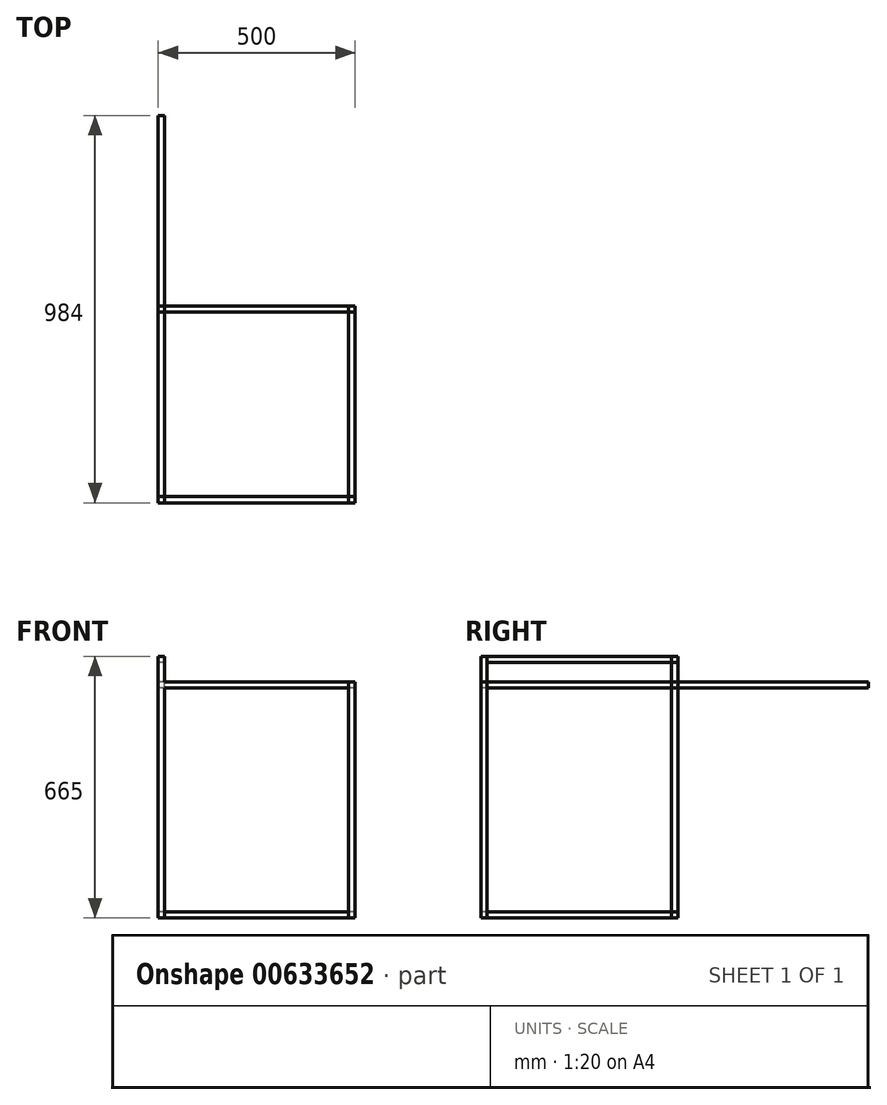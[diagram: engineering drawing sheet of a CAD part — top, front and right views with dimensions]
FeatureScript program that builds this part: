
annotation { "Feature Type Name" : "Feature", "Feature Type Description" : "" }
export const myFeature = defineFeature(function(context is Context, id is Id, definition is map)
    precondition{}
    {
        {
            var Q0;
            Q0=qCreatedBy(makeId("Front.planeOp"),FACE);
            var sketch = newSketch(context, id + "F0", { "sketchPlane" : qUnion([Q0])});
            skLineSegment(sketch, "E0.bottom", {"start": v(0, 0) * mm, "end": v(500, 0) * mm});
            skLineSegment(sketch, "E0.top", {"start": v(0, 600) * mm, "end": v(500, 600) * mm});
            skLineSegment(sketch, "E0.left", {"start": v(0, 0) * mm, "end": v(0, 600) * mm});
            skLineSegment(sketch, "E0.right", {"start": v(500, 0) * mm, "end": v(500, 600) * mm});
            skLineSegment(sketch, "E1.0", {"start": v(16, 584) * mm, "end": v(484, 584) * mm});
            skLineSegment(sketch, "E2.0", {"start": v(16, 0) * mm, "end": v(16, 600) * mm});
            skLineSegment(sketch, "E3.0", {"start": v(484, 0) * mm, "end": v(484, 600) * mm});
            skLineSegment(sketch, "E4.0", {"start": v(16, 16) * mm, "end": v(484, 16) * mm});
            skLineSegment(sketch, "E5.bottom", {"start": v(0, 600) * mm, "end": v(16, 600) * mm});
            skLineSegment(sketch, "E5.top", {"start": v(0, 665) * mm, "end": v(16, 665) * mm});
            skLineSegment(sketch, "E5.left", {"start": v(0, 600) * mm, "end": v(0, 665) * mm});
            skLineSegment(sketch, "E5.right", {"start": v(16, 600) * mm, "end": v(16, 665) * mm});
            skSolve(sketch);
        }
        {
            var Q0;
            Q0=qCreatedBy(makeId("Right.planeOp"),FACE);
            var sketch = newSketch(context, id + "F1", { "sketchPlane" : qUnion([Q0])});
            skLineSegment(sketch, "E6.bottom", {"start": v(16, 0) * mm, "end": v(500, 0) * mm});
            skLineSegment(sketch, "E6.top", {"start": v(16, 600) * mm, "end": v(500, 600) * mm});
            skLineSegment(sketch, "E7.0", {"start": v(16, 0) * mm, "end": v(16, 16) * mm});
            skLineSegment(sketch, "E8.0", {"start": v(500, 0) * mm, "end": v(500, 16) * mm});
            skLineSegment(sketch, "E9.0", {"start": v(16, 584) * mm, "end": v(500, 584) * mm});
            skLineSegment(sketch, "E10.0", {"start": v(16, 16) * mm, "end": v(500, 16) * mm});
            skLineSegment(sketch, "E11.trimOffspring", {"start": v(500, 584) * mm, "end": v(500, 600) * mm});
            skLineSegment(sketch, "E12.trimOffspring", {"start": v(16, 584) * mm, "end": v(16, 600) * mm});
            skLineSegment(sketch, "E13.0", {"start": v(16, 665) * mm, "end": v(500, 665) * mm});
            skLineSegment(sketch, "E14.0", {"start": v(16, 649) * mm, "end": v(500, 649) * mm});
            skLineSegment(sketch, "E15", {"start": v(500, 665) * mm, "end": v(500, 649) * mm});
            skLineSegment(sketch, "E16", {"start": v(16, 665) * mm, "end": v(16, 649) * mm});
            skSolve(sketch);
        }
        {
            var Q0;
            {var subQ4=sQuery(id+"F0.wireOp",EDGE,"E0.left");Q0=makeQuery(id+"F0.imprint","IMPRINT",FACE,{"disambiguationData":[TD([[makeQuery(id+"F0.imprint","IMPRINT",EDGE,{"derivedFrom":subQ4}),-1.0]])]});}
            var Q1;
            {var subQ0=sQuery(id+"F0.wireOp",EDGE,"E0.right");Q1=makeQuery(id+"F0.imprint","IMPRINT",FACE,{"disambiguationData":[TD([[makeQuery(id+"F0.imprint","IMPRINT",EDGE,{"derivedFrom":subQ0}),1.0]])]});}
            extrude(context, id + "F2", {"entities" : qUnion([Q0, Q1]), "depth" : -16 * mm, "offsetDistance" : 25 * mm});
        }
        {
            var Q0;
            {var subQ5=sQuery(id+"F0.wireOp",EDGE,"E1.0");Q0=makeQuery(id+"F0.imprint","IMPRINT",FACE,{"disambiguationData":[TD([[makeQuery(id+"F0.imprint","IMPRINT",EDGE,{"derivedFrom":subQ5}),1.0]])]});}
            var Q1;
            {var subQ5=sQuery(id+"F0.wireOp",EDGE,"E4.0");Q1=makeQuery(id+"F0.imprint","IMPRINT",FACE,{"disambiguationData":[TD([[makeQuery(id+"F0.imprint","IMPRINT",EDGE,{"derivedFrom":subQ5}),-1.0]])]});}
            extrude(context, id + "F3", {"entities" : qUnion([Q0, Q1]), "depth" : -16 * mm, "offsetDistance" : 25 * mm});
        }
        {
            var Q0;
            {var subQ0=sQuery(id+"F1.wireOp",EDGE,"E6.top");Q0=makeQuery(id+"F1.imprint","IMPRINT",FACE,{"disambiguationData":[TD([[makeQuery(id+"F1.imprint","IMPRINT",EDGE,{"derivedFrom":subQ0}),-1.0]])]});}
            var Q1;
            {var subQ0=sQuery(id+"F1.wireOp",EDGE,"E6.bottom");Q1=makeQuery(id+"F1.imprint","IMPRINT",FACE,{"disambiguationData":[TD([[makeQuery(id+"F1.imprint","IMPRINT",EDGE,{"derivedFrom":subQ0}),1.0]])]});}
            extrude(context, id + "F4", {"entities" : qUnion([Q0, Q1]), "depth" : 16 * mm, "offsetDistance" : 25 * mm});
        }
        {
            var Q0;
            Q0=makeQuery(id+"F2.opExtrude","SWEPT_BODY",BODY,{"disambiguationData":[OSD([sQuery(id+"F0.wireOp",EDGE,"E0.bottom"),sQuery(id+"F0.wireOp",EDGE,"E0.top"),sQuery(id+"F0.wireOp",EDGE,"E0.right"),sQuery(id+"F0.wireOp",EDGE,"E3.0")])]});
            var Q1;
            Q1=makeQuery(id+"F3.opExtrude","SWEPT_BODY",BODY,{"disambiguationData":[OSD([sQuery(id+"F0.wireOp",EDGE,"E0.top"),sQuery(id+"F0.wireOp",EDGE,"E1.0"),sQuery(id+"F0.wireOp",EDGE,"E2.0"),sQuery(id+"F0.wireOp",EDGE,"E3.0")])]});
            var Q2;
            Q2=makeQuery(id+"F3.opExtrude","SWEPT_BODY",BODY,{"disambiguationData":[OSD([sQuery(id+"F0.wireOp",EDGE,"E0.bottom"),sQuery(id+"F0.wireOp",EDGE,"E2.0"),sQuery(id+"F0.wireOp",EDGE,"E3.0"),sQuery(id+"F0.wireOp",EDGE,"E4.0")])]});
            var Q3;
            Q3=makeQuery(id+"F2.opExtrude","SWEPT_BODY",BODY,{"disambiguationData":[OSD([sQuery(id+"F0.wireOp",EDGE,"E0.bottom"),sQuery(id+"F0.wireOp",EDGE,"E0.top"),sQuery(id+"F0.wireOp",EDGE,"E0.left"),sQuery(id+"F0.wireOp",EDGE,"E2.0")])]});
            transform(context, id + "F5", {"entities" : qUnion([Q0, Q1, Q2, Q3]), "transformType" : TransformType.TRANSLATION_3D, "dx" : 0 * mm, "dy" : 484 * mm, "dz" : 0 * mm, "makeCopy" : true});
        }
        {
            var Q0;
            Q0=makeQuery(id+"F4.opExtrude","SWEPT_BODY",BODY,{"disambiguationData":[OSD([sQuery(id+"F1.wireOp",EDGE,"E6.top"),sQuery(id+"F1.wireOp",EDGE,"E7.0"),sQuery(id+"F1.wireOp",EDGE,"E8.0"),sQuery(id+"F1.wireOp",EDGE,"E9.0")])]});
            var Q1;
            Q1=makeQuery(id+"F4.opExtrude","SWEPT_BODY",BODY,{"disambiguationData":[OSD([sQuery(id+"F1.wireOp",EDGE,"E6.bottom"),sQuery(id+"F1.wireOp",EDGE,"E7.0"),sQuery(id+"F1.wireOp",EDGE,"E8.0"),sQuery(id+"F1.wireOp",EDGE,"E10.0")])]});
            transform(context, id + "F6", {"entities" : qUnion([Q0, Q1]), "transformType" : TransformType.TRANSLATION_3D, "dx" : 484 * mm, "dy" : 0 * mm, "dz" : 0 * mm, "makeCopy" : true});
        }
        {
            var Q0;
            Q0=makeQuery(id+"F0.imprint","IMPRINT",FACE,{"disambiguationData":[TD([[makeQuery(id+"F0.imprint","IMPRINT",EDGE,{"derivedFrom":sQuery(id+"F0.wireOp",EDGE,"E5.bottom")}),1.0]])]});
            extrude(context, id + "F7", {"entities" : qUnion([Q0]), "operationType" : NewBodyOperationType.ADD, "oppositeDirection" : true, "depth" : 16 * mm, "offsetDistance" : 25 * mm});
        }
        {
            var Q0;
            Q0=makeQuery(id+"F5.opPattern","COPY",BODY,{"derivedFrom":makeQuery(id+"F2.opExtrude","SWEPT_BODY",BODY,{"disambiguationData":[OSD([sQuery(id+"F0.wireOp",EDGE,"E0.bottom"),sQuery(id+"F0.wireOp",EDGE,"E0.right"),sQuery(id+"F0.wireOp",EDGE,"E3.0"),sQuery(id+"F0.wireOp",EDGE,"E5.bottom")])]}),"instanceName":"1"});
            deleteBodies(context, id + "F8", {"entities" : qUnion([Q0])});
        }
        {
            var Q0;
            Q0=makeQuery(id+"F2.opExtrude","SWEPT_BODY",BODY,{"disambiguationData":[OSD([sQuery(id+"F0.wireOp",EDGE,"E0.bottom"),sQuery(id+"F0.wireOp",EDGE,"E0.right"),sQuery(id+"F0.wireOp",EDGE,"E3.0"),sQuery(id+"F0.wireOp",EDGE,"E5.bottom")])]});
            transform(context, id + "F9", {"entities" : qUnion([Q0]), "transformType" : TransformType.TRANSLATION_3D, "dx" : 0 * mm, "dy" : 484 * mm, "dz" : 0 * mm, "makeCopy" : true});
        }
        {
            var Q0;
            Q0=makeQuery(id+"F1.imprint","IMPRINT",FACE,{"disambiguationData":[TD([[makeQuery(id+"F1.imprint","IMPRINT",EDGE,{"derivedFrom":sQuery(id+"F1.wireOp",EDGE,"E13.0")}),-1.0]])]});
            extrude(context, id + "F10", {"entities" : qUnion([Q0]), "depth" : 16 * mm, "offsetDistance" : 25 * mm});
        }
        {
            var Q0;
            Q0=makeQuery(id+"F5.opPattern","COPY",BODY,{"derivedFrom":makeQuery(id+"F2.opExtrude","SWEPT_BODY",BODY,{"disambiguationData":[OSD([sQuery(id+"F0.wireOp",EDGE,"E0.bottom"),sQuery(id+"F0.wireOp",EDGE,"E0.left"),sQuery(id+"F0.wireOp",EDGE,"E2.0"),sQuery(id+"F0.wireOp",EDGE,"E5.bottom")])]}),"instanceName":"1"});
            deleteBodies(context, id + "F11", {"entities" : qUnion([Q0])});
        }
        {
            var Q0;
            Q0=makeQuery(id+"F2.opExtrude","SWEPT_BODY",BODY,{"disambiguationData":[OSD([sQuery(id+"F0.wireOp",EDGE,"E0.bottom"),sQuery(id+"F0.wireOp",EDGE,"E0.left"),sQuery(id+"F0.wireOp",EDGE,"E2.0"),sQuery(id+"F0.wireOp",EDGE,"E5.bottom")])]});
            transform(context, id + "F12", {"entities" : qUnion([Q0]), "transformType" : TransformType.TRANSLATION_3D, "dx" : 0 * mm, "dy" : 484 * mm, "dz" : 0 * mm, "makeCopy" : true});
        }
    });
